FCSTD DOCUMENT  (FreeCAD 0.16R6700 (Git))
Label: pulley2
License: All rights reserved
LicenseURL: http://en.wikipedia.org/wiki/All_rights_reserved
objects: Sketcher::SketchObject×6, PartDesign::Pad×3, Part::Cut×2, PartDesign::Pocket×2, Part::Helix×1, Part::Sweep×1, PartDesign::Fillet×1, Mesh::Feature×1
note: 21 computed .brp shape members not serialized (recipe doc carries the construction recipe); baked Part::Feature solids carry a one-line shape summary decoded from their .brp

FEATURE [Sketcher::SketchObject] Sketch
  sketch-geometry (1):
    g0: Circle CenterX=0 CenterY=0 CenterZ=0 NormalX=0 NormalY=0 NormalZ=1 Radius=15
  constraints (2):
    c: Coincident(g0,g-1)
    c: Radius(g0) = 15
FEATURE [PartDesign::Pad] Pad
  Length = 40
  Length2 = 100
  Reversed = true
  Sketch = -> Sketch
  Type = 0
FEATURE [Part::Helix] Helix
  Angle = 0
  Height = 40
  LocalCoord = 0
  Pitch = 2
  Placement = pos=(0,0,-40) rot=(0,0,1;0rad)
  Radius = 15
  Style = 1
FEATURE [Sketcher::SketchObject] Sketch001
  Placement = pos=(0,0,0) rot=(-1,0,0;4.71239rad)
  sketch-geometry (1):
    g0: Circle CenterX=15 CenterY=0 CenterZ=0 NormalX=0 NormalY=0 NormalZ=1 Radius=0.75
  constraints (3):
    c: Radius(g0) = 0.75
    c: PointOnObject(g0,g-1)
    c: DistanceX(g-1,g0) = 15
FEATURE [Part::Sweep] Sweep
  Frenet = false
  Sections = -> [Sketch001]
  Solid = true
  Spine = -> Helix
  Transition = 1
FEATURE [Part::Cut] Cut  label="screw"
  Base = -> Pad
  Tool = -> Sweep
FEATURE [Sketcher::SketchObject] Sketch002
  Placement = pos=(0,0,0) rot=(-1,0,0;4.71239rad)
  sketch-geometry (1):
    g0: Circle CenterX=0 CenterY=-20 CenterZ=0 NormalX=0 NormalY=0 NormalZ=1 Radius=1.5
  constraints (3):
    c: Radius(g0) = 1.5
    c: PointOnObject(g0,g-2)
    c: DistanceY(g0,g-1) = 20
FEATURE [PartDesign::Pad] Pad001  label="hole"
  Length = 40
  Length2 = 100
  Midplane = true
  Placement = pos=(0,0,0) rot=(-1,0,0;4.71239rad)
  Sketch = -> Sketch002
  Type = 0
FEATURE [Part::Cut] Cut001
  Base = -> Cut
  Tool = -> Pad001
FEATURE [Sketcher::SketchObject] Sketch003
  Placement = pos=(0,0,-40) rot=(1,0,0;3.14159rad)
  Support = -> Cut001 [Face58]
  sketch-geometry (1):
    g0: Circle CenterX=0 CenterY=0 CenterZ=0 NormalX=0 NormalY=0 NormalZ=1 Radius=10
  constraints (2):
    c: Coincident(g0,g-1)
    c: Radius(g0) = 10
FEATURE [PartDesign::Pocket] Pocket
  Length = 25
  Sketch = -> Sketch003
  Type = 0
FEATURE [Sketcher::SketchObject] Sketch004
  Placement = pos=(0,0,-40) rot=(1,0,0;3.14159rad)
  Support = -> Pocket [Face33]
  sketch-geometry (2):
    g0: Circle CenterX=0 CenterY=0 CenterZ=0 NormalX=0 NormalY=0 NormalZ=1 Radius=10
    g1: Circle CenterX=0 CenterY=0 CenterZ=0 NormalX=0 NormalY=0 NormalZ=1 Radius=17
  constraints (4):
    c: Coincident(g0,g-1)
    c: Radius(g0) = 10
    c: Radius(g1) = 17
    c: Coincident(g0,g1)
FEATURE [PartDesign::Pad] Pad002
  Length = 10
  Length2 = 100
  Sketch = -> Sketch004
  Type = 0
FEATURE [Sketcher::SketchObject] Sketch005
  Placement = pos=(0,0,-50) rot=(1,0,0;3.14159rad)
  Support = -> Pad002 [Face37]
  sketch-geometry (1):
    g0: Circle CenterX=0 CenterY=0 CenterZ=0 NormalX=0 NormalY=0 NormalZ=1 Radius=12
  constraints (2):
    c: Coincident(g0,g-1)
    c: Radius(g0) = 12
FEATURE [PartDesign::Pocket] Pocket001
  Length = 5
  Sketch = -> Sketch005
  Type = 0
FEATURE [PartDesign::Fillet] Fillet
  Base = -> Pocket001 [Edge143]
  Radius = 1.5
FEATURE [Mesh::Feature] pulley_full_w_bearing_cut
  Placement = pos=(0,0,10) rot=(1,0,0;3.14159rad)
